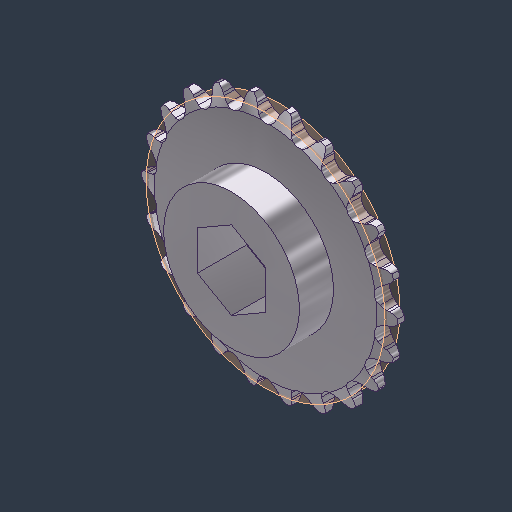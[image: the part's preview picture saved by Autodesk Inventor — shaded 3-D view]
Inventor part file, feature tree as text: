
AUTODESK INVENTOR PART (.ipt)
format: ipt  version: 2024.3 (Build 283343000, 343)  size: 578,560 bytes
history: native  units: mm (DEFAULTED — no unit token found)
features: other x2, sketch x1, extrude x1
ambient origin geometry x8: Origin, YZ Plane, XZ Plane, XY Plane, X Axis, Y Axis, Z Axis, Center Point
bodies: Solid1 (feature_tree)
feature tree (4):
  sketch  "Sketch3"  dims[d10=44.704mm d11=25.4mm d12=0.0mm]
  other  "Srf1"
  other  "Cut-Extrude2"
  extrude  "ExtrusionSrf1"  Depth=25.4mm TaperAngle=0.0deg
